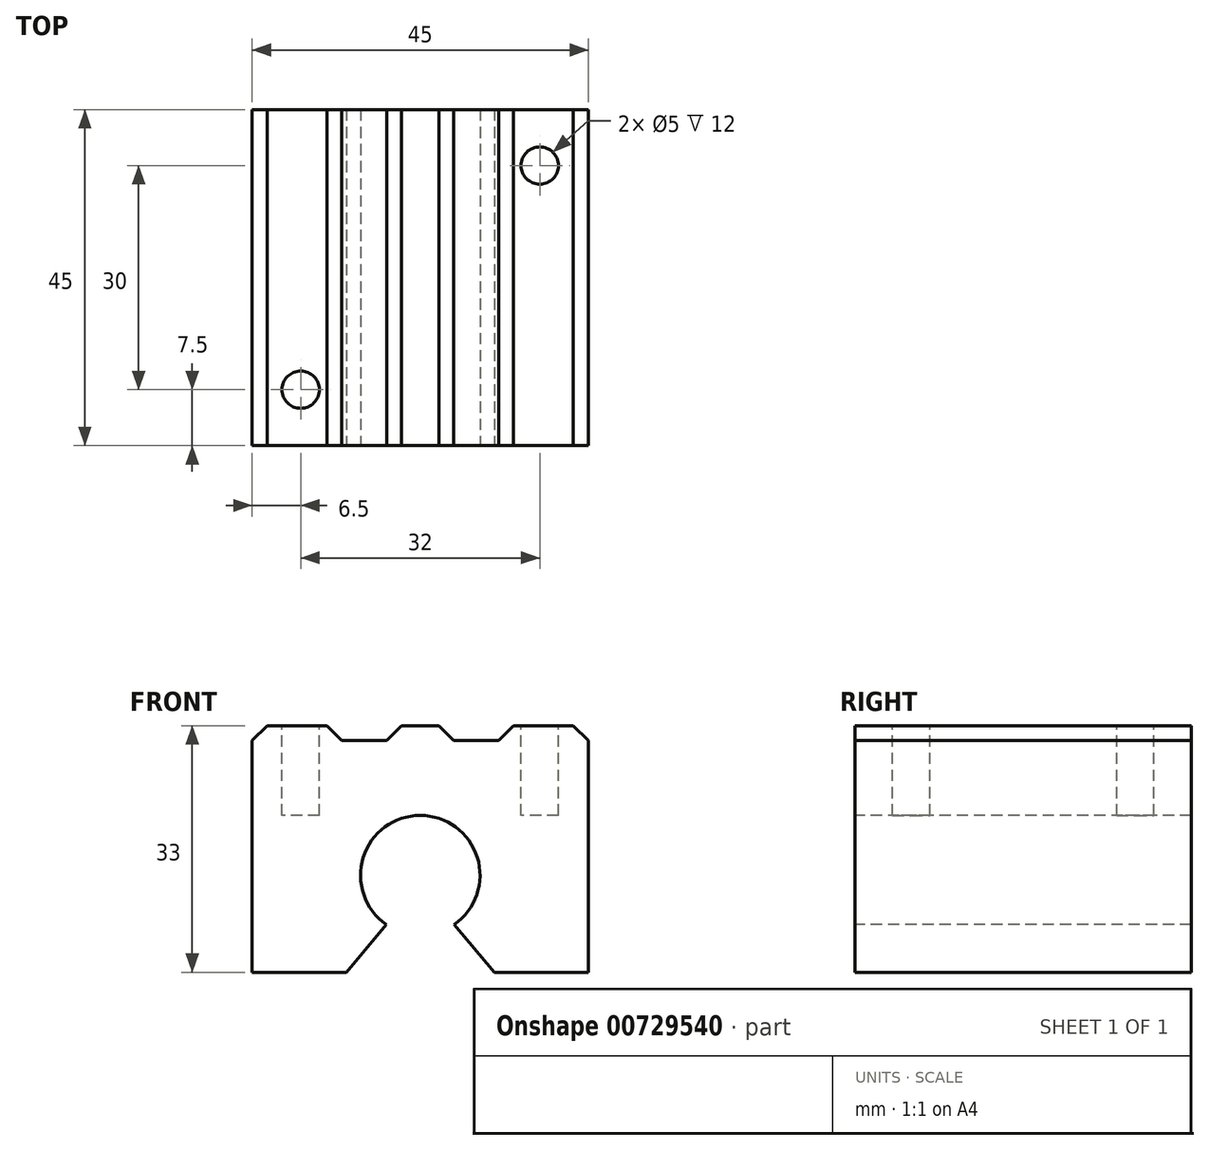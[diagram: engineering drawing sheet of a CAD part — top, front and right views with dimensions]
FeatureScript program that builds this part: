
annotation { "Feature Type Name" : "Feature", "Feature Type Description" : "" }
export const myFeature = defineFeature(function(context is Context, id is Id, definition is map)
    precondition{}
    {
        {
            var Q0;
            Q0=qCreatedBy(makeId("Front.planeOp"),FACE);
            var sketch = newSketch(context, id + "F0", { "sketchPlane" : qUnion([Q0])});
            skArc(sketch, "E0", {"start": v(4.53, -6.6) * mm, "mid": v(0, 8) * mm, "end": v(-4.53, -6.6) * mm});
            skLineSegment(sketch, "E1", {"start": v(0, 33.95) * mm, "end": v(0, -22.88) * mm, "construction": true});
            skLineSegment(sketch, "E2", {"start": v(0, 20) * mm, "end": v(2.5, 20) * mm});
            skLineSegment(sketch, "E3", {"start": v(22.5, 20) * mm, "end": v(22.5, -13) * mm});
            skLineSegment(sketch, "E4.MirrorCS", {"start": v(0, 20) * mm, "end": v(-2.5, 20) * mm});
            skLineSegment(sketch, "E5.MirrorCS", {"start": v(-22.5, 20) * mm, "end": v(-22.5, -13) * mm});
            skPoint(sketch, "E6.orphan", {"position": v(0, 30.01) * mm});
            skLineSegment(sketch, "E7", {"start": v(2.5, 20) * mm, "end": v(4.5, 18) * mm});
            skLineSegment(sketch, "E8", {"start": v(4.5, 18) * mm, "end": v(10.5, 18) * mm});
            skLineSegment(sketch, "E9", {"start": v(10.5, 18) * mm, "end": v(12.5, 20) * mm});
            skLineSegment(sketch, "E10.MirrorCS", {"start": v(-2.5, 20) * mm, "end": v(-4.5, 18) * mm});
            skLineSegment(sketch, "E11.MirrorCS", {"start": v(-4.5, 18) * mm, "end": v(-10.5, 18) * mm});
            skLineSegment(sketch, "E12.MirrorCS", {"start": v(-10.5, 18) * mm, "end": v(-12.5, 20) * mm});
            skLineSegment(sketch, "E13.trimOffspring", {"start": v(12.5, 20) * mm, "end": v(22.5, 20) * mm});
            skLineSegment(sketch, "E14.trimOffspring", {"start": v(-12.5, 20) * mm, "end": v(-22.5, 20) * mm});
            skLineSegment(sketch, "E15", {"start": v(-22.5, -13) * mm, "end": v(-9.9, -13) * mm});
            skLineSegment(sketch, "E16", {"start": v(-4.53, -6.6) * mm, "end": v(-9.9, -13) * mm});
            skLineSegment(sketch, "E17.MirrorCS", {"start": v(4.53, -6.6) * mm, "end": v(9.9, -13) * mm});
            skPoint(sketch, "E18.end.orphan", {"position": v(4.53, -6.6) * mm});
            skLineSegment(sketch, "E19.trimOffspring", {"start": v(9.9, -13) * mm, "end": v(22.5, -13) * mm});
            skSolve(sketch);
        }
        {
            var Q0;
            Q0=makeQuery(id+"F0.imprint","IMPRINT",FACE,{"disambiguationData":[TD([[makeQuery(id+"F0.imprint","IMPRINT",EDGE,{"derivedFrom":sQuery(id+"F0.wireOp",EDGE,"E0")}),-1.0]])]});
            extrude(context, id + "F1", {"entities" : qUnion([Q0]), "oppositeDirection" : true, "depth" : 45 * mm, "offsetDistance" : 25 * mm});
        }
        {
            var Q0;
            Q0=makeQuery(id+"F1.opExtrude","SWEPT_FACE",FACE,{"disambiguationData":[OSD([sQuery(id+"F0.wireOp",EDGE,"E2"),sQuery(id+"F0.wireOp",EDGE,"E4.MirrorCS")])]});
            var sketch = newSketch(context, id + "F2", { "sketchPlane" : qUnion([Q0])});
            skLineSegment(sketch, "E20.bottom", {"start": v(0, 37.5) * mm, "end": v(16, 37.5) * mm, "construction": true});
            skLineSegment(sketch, "E20.right", {"start": v(16, 37.5) * mm, "end": v(16, 22.5) * mm, "construction": true});
            skCircle(sketch, "E21", {"center": v(16, 37.5) * mm, "radius": 2.5 * mm});
            skLineSegment(sketch, "E22", {"start": v(0, 67.54) * mm, "end": v(0, -5.3) * mm, "construction": true});
            skLineSegment(sketch, "E23", {"start": v(-43.18, 22.5) * mm, "end": v(57.19, 22.5) * mm, "construction": true});
            skCircle(sketch, "E24.MirrorC", {"center": v(-16, 37.5) * mm, "radius": 2.5 * mm});
            skCircle(sketch, "E25.MirrorC", {"center": v(-16, 7.5) * mm, "radius": 2.5 * mm});
            skCircle(sketch, "E26.MirrorC", {"center": v(16, 7.5) * mm, "radius": 2.5 * mm});
            skSolve(sketch);
        }
        {
            var Q0;
            Q0=makeQuery(id+"F1.opExtrude","SWEPT_EDGE",EDGE,{"disambiguationData":[OSD([sQuery(id+"F0.wireOp",EDGE,"E3"),sQuery(id+"F0.wireOp",EDGE,"E13.trimOffspring")])]});
            var Q1;
            Q1=makeQuery(id+"F1.opExtrude","SWEPT_EDGE",EDGE,{"disambiguationData":[OSD([sQuery(id+"F0.wireOp",EDGE,"E5.MirrorCS"),sQuery(id+"F0.wireOp",EDGE,"E14.trimOffspring")])]});
            chamfer(context, id + "F3", {"entities" : qUnion([Q0, Q1]), "width" : 2 * mm, "tangentPropagation" : true});
        }
        {
            var Q0;
            Q0=makeQuery(id+"F2.imprint","IMPRINT",FACE,{"disambiguationData":[TD([[makeQuery(id+"F2.imprint","IMPRINT",EDGE,{"derivedFrom":sQuery(id+"F2.wireOp",EDGE,"E24.MirrorC")}),-1.0]])]});
            var Q1;
            Q1=makeQuery(id+"F2.imprint","IMPRINT",FACE,{"disambiguationData":[TD([[makeQuery(id+"F2.imprint","IMPRINT",EDGE,{"derivedFrom":sQuery(id+"F2.wireOp",EDGE,"E25.MirrorC")}),1.0]])]});
            var Q2;
            Q2=makeQuery(id+"F2.imprint","IMPRINT",FACE,{"disambiguationData":[TD([[makeQuery(id+"F2.imprint","IMPRINT",EDGE,{"derivedFrom":sQuery(id+"F2.wireOp",EDGE,"E21")}),1.0]])]});
            var Q3;
            Q3=makeQuery(id+"F2.imprint","IMPRINT",FACE,{"disambiguationData":[TD([[makeQuery(id+"F2.imprint","IMPRINT",EDGE,{"derivedFrom":sQuery(id+"F2.wireOp",EDGE,"E26.MirrorC")}),-1.0]])]});
            extrude(context, id + "F4", {"entities" : qUnion([Q0, Q1, Q2, Q3]), "operationType" : NewBodyOperationType.REMOVE, "oppositeDirection" : true, "depth" : 12 * mm, "offsetDistance" : 25 * mm});
        }
    });
